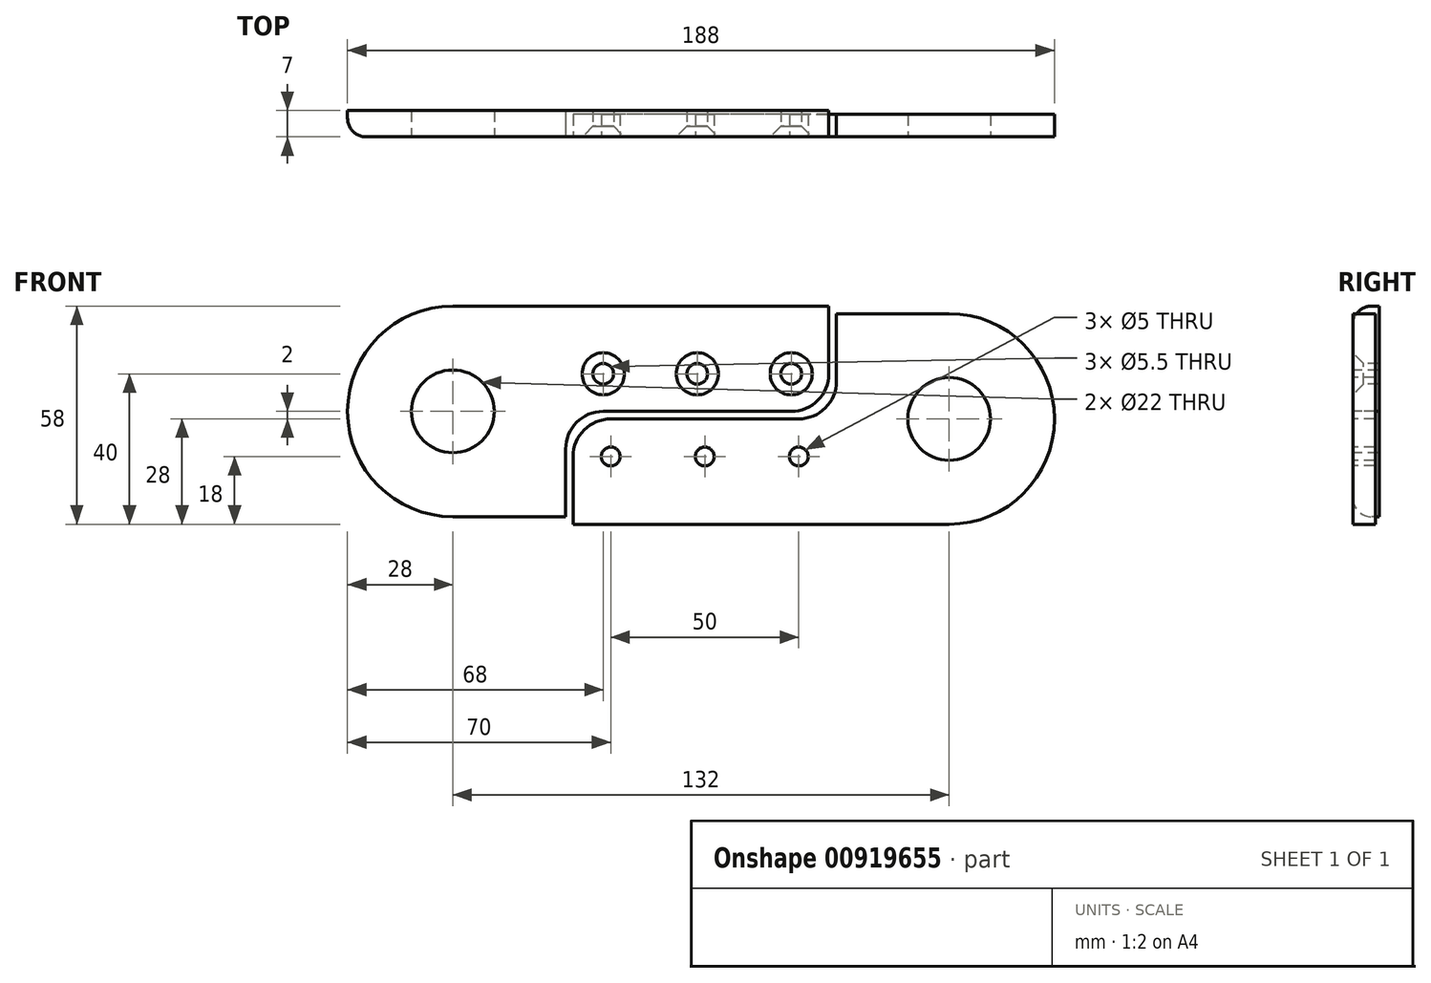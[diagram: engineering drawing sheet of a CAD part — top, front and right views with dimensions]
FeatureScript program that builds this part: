
annotation { "Feature Type Name" : "Feature", "Feature Type Description" : "" }
export const myFeature = defineFeature(function(context is Context, id is Id, definition is map)
    precondition{}
    {
        {
            var Q0;
            Q0=qCreatedBy(makeId("Front.planeOp"),FACE);
            var sketch = newSketch(context, id + "F0", { "sketchPlane" : qUnion([Q0])});
            skCircle(sketch, "E0", {"center": v(0, 0) * mm, "radius": 11 * mm});
            skLineSegment(sketch, "E1.bottom", {"start": v(0, 28) * mm, "end": v(100, 28) * mm});
            skArc(sketch, "E2", {"start": v(0, -28) * mm, "mid": v(-28, 0) * mm, "end": v(0, 28) * mm});
            skLineSegment(sketch, "E3", {"start": v(30, -28) * mm, "end": v(0, -28) * mm});
            skLineSegment(sketch, "E4.top", {"start": v(40, 0) * mm, "end": v(90, 0) * mm});
            skLineSegment(sketch, "E4.right", {"start": v(100, 28) * mm, "end": v(100, 10) * mm});
            skLineSegment(sketch, "E5", {"start": v(30, -10) * mm, "end": v(30, -28) * mm});
            skLineSegment(sketch, "E6", {"start": v(40, 10) * mm, "end": v(90, 10) * mm, "construction": true});
            skPoint(sketch, "E7", {"position": v(65, 10) * mm});
            skPoint(sketch, "E8.visualSharp", {"position": v(30, 0) * mm});
            skArc(sketch, "E8.filletArc", {"start": v(40, 0) * mm, "mid": v(32.93, -2.93) * mm, "end": v(30, -10) * mm});
            skPoint(sketch, "E9.visualSharp", {"position": v(100, 0) * mm});
            skArc(sketch, "E9.filletArc", {"start": v(90, 0) * mm, "mid": v(97.07, 2.93) * mm, "end": v(100, 10) * mm});
            skCircle(sketch, "E10", {"center": v(40, 10) * mm, "radius": 2.5 * mm});
            skCircle(sketch, "E11", {"center": v(65, 10) * mm, "radius": 2.5 * mm});
            skCircle(sketch, "E12", {"center": v(90, 10) * mm, "radius": 2.5 * mm});
            skPoint(sketch, "E13.1.0", {"position": v(102, -2) * mm});
            skPoint(sketch, "E13.1.1", {"position": v(32, -2) * mm});
            skLineSegment(sketch, "E13.1.2", {"start": v(132, -30) * mm, "end": v(32, -30) * mm});
            skLineSegment(sketch, "E13.1.3", {"start": v(92, -2) * mm, "end": v(42, -2) * mm});
            skLineSegment(sketch, "E13.1.4", {"start": v(102, 26) * mm, "end": v(132, 26) * mm});
            skCircle(sketch, "E13.1.5", {"center": v(132, -2) * mm, "radius": 11 * mm});
            skPoint(sketch, "E13.1.6", {"position": v(67, -12) * mm});
            skLineSegment(sketch, "E13.1.7", {"start": v(102, 8) * mm, "end": v(102, 26) * mm});
            skArc(sketch, "E13.1.8", {"start": v(132, 26) * mm, "mid": v(160, -2) * mm, "end": v(132, -30) * mm});
            skLineSegment(sketch, "E13.1.9", {"start": v(92, -12) * mm, "end": v(42, -12) * mm, "construction": true});
            skLineSegment(sketch, "E13.1.10", {"start": v(32, -30) * mm, "end": v(32, -12) * mm});
            skCircle(sketch, "E13.1.11", {"center": v(67, -12) * mm, "radius": 2.5 * mm});
            skArc(sketch, "E13.1.12", {"start": v(42, -2) * mm, "mid": v(34.93, -4.93) * mm, "end": v(32, -12) * mm});
            skArc(sketch, "E13.1.13", {"start": v(92, -2) * mm, "mid": v(99.07, 0.93) * mm, "end": v(102, 8) * mm});
            skCircle(sketch, "E13.1.14", {"center": v(92, -12) * mm, "radius": 2.5 * mm});
            skCircle(sketch, "E13.1.15", {"center": v(42, -12) * mm, "radius": 2.5 * mm});
            skPoint(sketch, "E13.center", {"position": v(66, -1) * mm});
            skSolve(sketch);
        }
        {
            var Q0;
            Q0=makeQuery(id+"F0.imprint","IMPRINT",FACE,{"disambiguationData":[TD([[makeQuery(id+"F0.imprint","IMPRINT",EDGE,{"derivedFrom":sQuery(id+"F0.wireOp",EDGE,"E0")}),-1.0]])]});
            extrude(context, id + "F1", {"entities" : qUnion([Q0]), "oppositeDirection" : true, "depth" : 7 * mm, "offsetDistance" : 25 * mm});
        }
        {
            var Q0;
            Q0=makeQuery(id+"F1.opExtrude","CAP_EDGE",EDGE,{"disambiguationData":[OSD([sQuery(id+"F0.wireOp",EDGE,"E1.bottom")])],"isStart":true});
            fillet(context, id + "F2", {"entities" : qUnion([Q0]), "radius" : 5 * mm, "tangentPropagation" : true, "allowEdgeOverflow" : false});
        }
        {
            var Q0;
            Q0=sQuery(id+"F0.wireOp",VERTEX,"E6.end");
            var Q1;
            Q1=sQuery(id+"F0.wireOp",VERTEX,"E7");
            var Q2;
            Q2=sQuery(id+"F0.wireOp",VERTEX,"E6.start");
            var Q3;
            Q3=makeQuery(id+"F1.opExtrude","SWEPT_BODY",BODY,{"disambiguationData":[OSD([sQuery(id+"F0.wireOp",EDGE,"E0"),sQuery(id+"F0.wireOp",EDGE,"E1.bottom"),sQuery(id+"F0.wireOp",EDGE,"E2"),sQuery(id+"F0.wireOp",EDGE,"E3"),sQuery(id+"F0.wireOp",EDGE,"E4.top"),sQuery(id+"F0.wireOp",EDGE,"E4.right"),sQuery(id+"F0.wireOp",EDGE,"E5"),sQuery(id+"F0.wireOp",EDGE,"E8.filletArc"),sQuery(id+"F0.wireOp",EDGE,"E9.filletArc")])]});
            hole(context, id + "F3", {"style" : HoleStyle.C_SINK, "endStyle" : HoleEndStyle.THROUGH, "standardTappedOrClearance" : lookupTablePath({ "fit" : "Normal", "standard" : "ISO", "size" : "M5", "type" : "Clearance" }), "standardBlindInLast" : lookupTablePath({ "fit" : "Normal", "standard" : "ISO", "engagement" : "75%", "pitch" : "0.8 mm", "size" : "M5", "type" : "Clearance & tapped" }), "holeDiameter" : 5.5 * mm, "cSinkDiameter" : 11.2 * mm, "cSinkAngle" : 90 * degree, "majorDiameter" : 5 * mm, "isTappedThrough" : true, "tappedDepth" : 12 * mm, "tapClearance" : 3, "locations" : qUnion([Q0, Q1, Q2]), "scope" : qUnion([Q3])});
        }
        {
            var Q0;
            Q0=makeQuery(id+"F0.imprint","IMPRINT",FACE,{"disambiguationData":[TD([[makeQuery(id+"F0.imprint","IMPRINT",EDGE,{"derivedFrom":sQuery(id+"F0.wireOp",EDGE,"E13.1.2")}),-1.0]])]});
            extrude(context, id + "F4", {"entities" : qUnion([Q0]), "oppositeDirection" : true, "depth" : 6 * mm, "offsetDistance" : 25 * mm});
        }
    });
